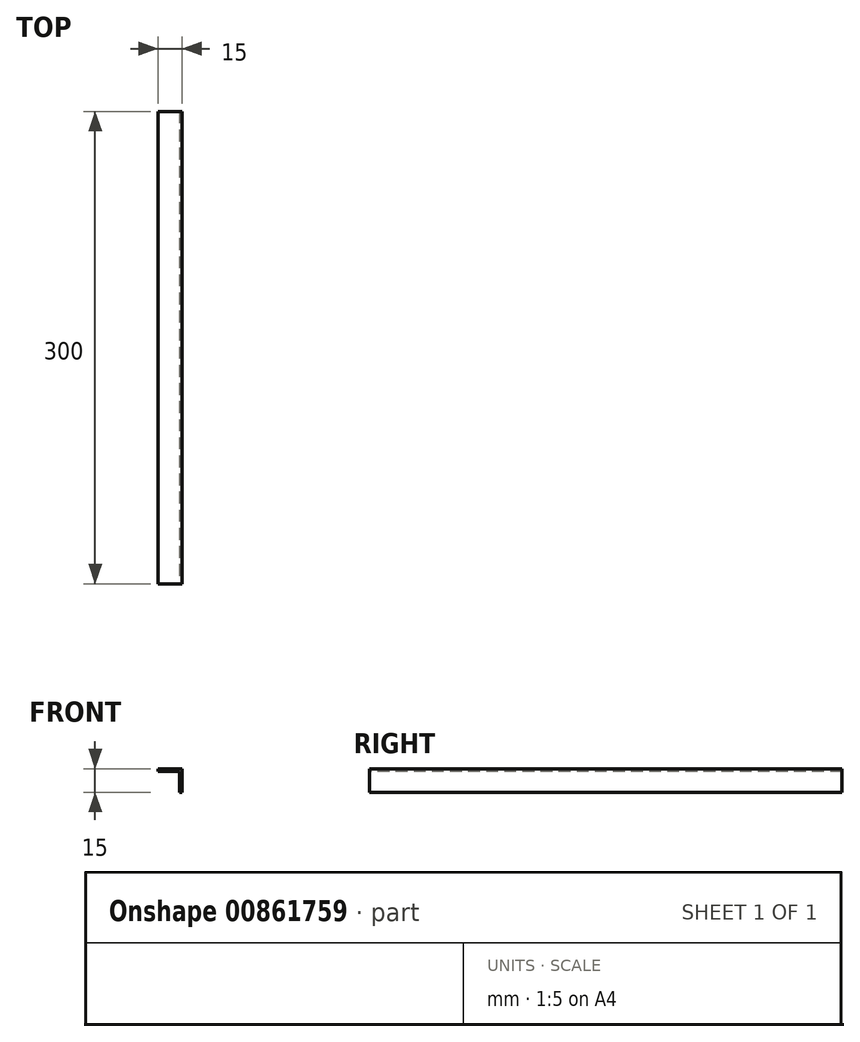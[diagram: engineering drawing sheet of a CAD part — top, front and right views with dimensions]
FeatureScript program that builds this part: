
annotation { "Feature Type Name" : "Feature", "Feature Type Description" : "" }
export const myFeature = defineFeature(function(context is Context, id is Id, definition is map)
    precondition{}
    {
        {
            var Q0;
            Q0=qCreatedBy(makeId("Front.planeOp"),FACE);
            var sketch = newSketch(context, id + "F0", { "sketchPlane" : qUnion([Q0])});
            skLineSegment(sketch, "E0", {"start": v(-21.04, 13.9) * mm, "end": v(-21.04, -1.1) * mm});
            skLineSegment(sketch, "E1", {"start": v(-21.04, -1.1) * mm, "end": v(-6.04, -1.1) * mm});
            skLineSegment(sketch, "E2", {"start": v(-6.04, -1.1) * mm, "end": v(-6.04, 0.5) * mm});
            skLineSegment(sketch, "E3", {"start": v(-6.04, 0.5) * mm, "end": v(-19.44, 0.5) * mm});
            skLineSegment(sketch, "E4", {"start": v(-19.44, 0.5) * mm, "end": v(-19.44, 13.87) * mm});
            skLineSegment(sketch, "E5", {"start": v(-19.44, 13.87) * mm, "end": v(-21.04, 13.9) * mm});
            skSolve(sketch);
        }
        {
            var Q0;
            Q0=makeQuery(id+"F0.imprint","IMPRINT",FACE,{"disambiguationData":[TD([[makeQuery(id+"F0.imprint","IMPRINT",EDGE,{"derivedFrom":sQuery(id+"F0.wireOp",EDGE,"E0")}),1.0]])]});
            extrude(context, id + "F1", {"entities" : qUnion([Q0]), "endBound" : BoundingType.SYMMETRIC, "oppositeDirection" : true, "depth" : 300 * mm, "offsetDistance" : 25 * mm});
        }
        {
            var Q0;
            Q0=makeQuery(id+"F1.opExtrude","SWEPT_BODY",BODY,{"disambiguationData":[OSD([sQuery(id+"F0.wireOp",EDGE,"E0"),sQuery(id+"F0.wireOp",EDGE,"E1"),sQuery(id+"F0.wireOp",EDGE,"E2"),sQuery(id+"F0.wireOp",EDGE,"E3"),sQuery(id+"F0.wireOp",EDGE,"E4"),sQuery(id+"F0.wireOp",EDGE,"E5")])]});
            var Q1;
            Q1=makeQuery(id+"F1.opExtrude","SWEPT_EDGE",EDGE,{"disambiguationData":[OSD([sQuery(id+"F0.wireOp",EDGE,"E0"),sQuery(id+"F0.wireOp",EDGE,"E1")])]});
            transform(context, id + "F2", {"entities" : qUnion([Q0]), "transformType" : TransformType.ROTATION, "transformAxis" : qUnion([Q1]), "angle" : 180 * degree, "makeCopy" : false});
        }
    });
